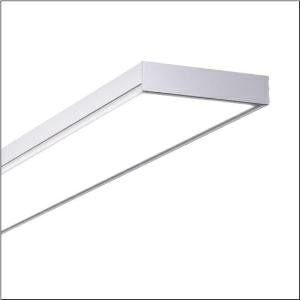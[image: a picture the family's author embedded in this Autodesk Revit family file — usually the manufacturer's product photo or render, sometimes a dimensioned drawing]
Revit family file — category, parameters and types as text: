
# Revit family: apollon_31_surface_51mp26wm2441ea
name_source: partatom
category: Lighting Fixtures
units: mm (PartAtom-declared; Revit-internal decimal feet)

## family parameters
Cut with Voids When Loaded = No
Host = Face
Light Source = No
Part Type = Normal
Room Calculation Point = No
Round Connector Dimension = Use Diameter
Shared = No

## types (1)
- Apollon 31 Surface (1 x LED, 4600 lm, 33 W, 4000K)
    Apparent Load = 33 VA
    CIE Flux Codes = 61 87 97 97 100
    Color Rendering = 80
    Color Temperature = 4000K
    Default Elevation = 1800 mm
    Description = Apollon 31 Surface, office luminaire, primary optical cover: micro prismatic cover, of PMMA, light emission: direct distribution, primary light characteristic: symmetric, installation type: surface-mounted, LED, rated luminous flux: 4.600lm, luminous efficacy: 139lm/W, light colour: 840, colour temperature: 4000K, control gear: ON/OFF Multilumen, with terminal, 3-pole, mains connection: 220..240V, AC, 50/60Hz, rated input power: 33W, housing, of sheet steel, coated, metallic grey (RAL 9006), length: 1.545mm, width: 200mm, height: 44mm, protection rating (complete): IP20, protection rating (on room side): IP40, protection rating (lamp compartment, on room side): IP40, insulation class (complete): insulation class I (protective earthing), certification: CE, ENEC, UKCA, impact resistance: IK02, permissible operating ambient temperature: -20..+40°C, packaging unit: 1 piece
    Height = 44 mm
    Lamp = 1 x LED
    Lamp Light Flux = 4600 lm
    Lamp Power = 33 W
    Lamp count = 1
    Length = 1545 mm
    Luminous efficacy = 139 lm/W
    Manufacturer = Siteco
    ModVariant = No
    Model = 51MP26WM2441EA
    Mounting Place = Ceiling
    Mounting Type = Surface mounted
    Number of Poles = 1
    OnlyDefault = Yes
    Power Factor = 1
    Product Name = Apollon 31 Surface
    Product group = office luminaire | ceiling mounted
    ProductGroupID = 301
    Protection Class = Protection class I
    Protection Degree = IP 20
    RLX_Detail_Level = 1
    RLX_Emergency_Light_Flux = 0 lm
    RLX_Emergency_Type = 0
    RLX_Emergency_Type_DB = No
    RlxData = <blob elided: 24161 chars, md5=4ad2243b>
    Socket = socket
    Standby Power = 0 W
    System Light Flux = 4600 lm
    System Power = 33 W
    Type Comments = Product without accessories
    Type Image = l_1313654.jpg
    URL = http://relux.com
    VarID = ---
    Voltage = 0 V
    Weight = 0.00 kg
    Width = 200 mm  [stored 0.656168 ft]

note: [stored X ft] marks values corroborated as IEEE doubles in the binary element streams (Revit-internal decimal feet)

## geometry (parser evidence)
native form markers: Blend x4, Sweep x11
no freeform markers — native parametric forms only
